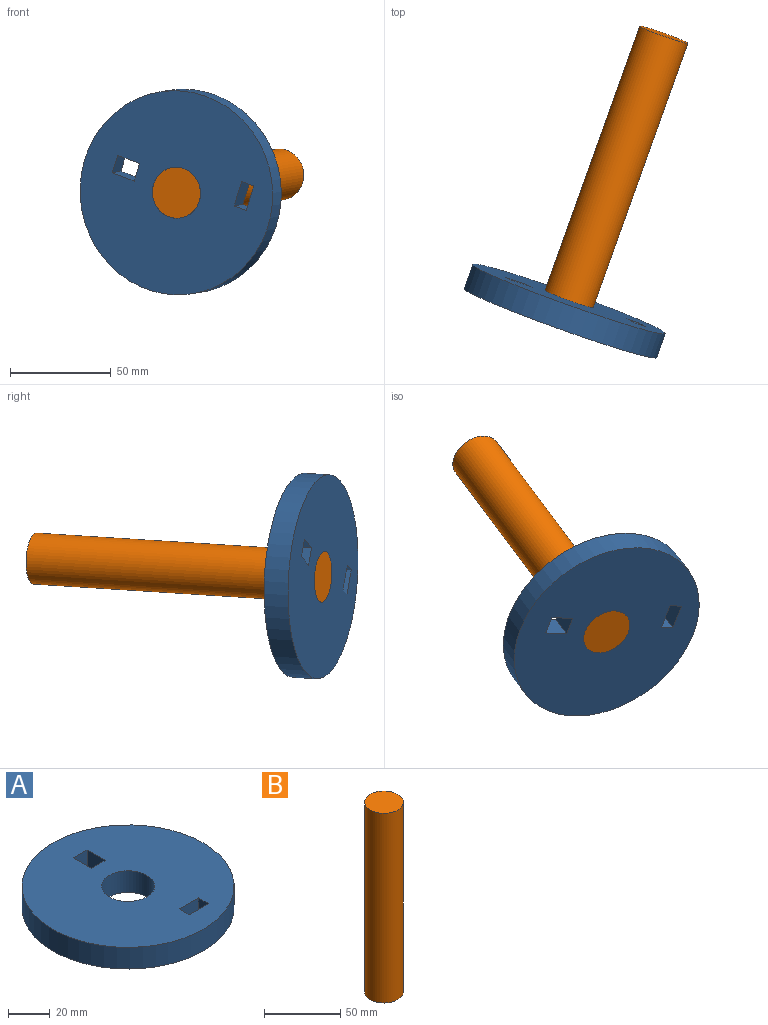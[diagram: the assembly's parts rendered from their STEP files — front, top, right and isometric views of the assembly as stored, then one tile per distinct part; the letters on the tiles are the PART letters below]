
ASSEMBLY  parts=2 mates=1
PART A: 12 faces, bbox 101.6x101.6x12.7 mm
  f0: plane 13.01x12.7mm, normal (0,1,0), area 165.2mm2, adj f1,f6,f10,f11
  f1: plane 12.7x6.7mm, normal (1,0,0), area 85.1mm2, adj f0,f2,f10,f11
  f2: plane 13.01x12.7mm, normal (0,-1,0), area 165.2mm2, adj f1,f6,f10,f11
  f3: plane 12.7x9.26mm, normal (0,1,0), area 117.6mm2, adj f4,f7,f10,f11
  f4: plane 12.7x12.22mm, normal (1,0,0), area 155.2mm2, adj f3,f5,f10,f11
  f5: plane 12.7x9.26mm, normal (0,-1,0), area 117.6mm2, adj f4,f7,f10,f11
  f6: plane 12.7x6.7mm, normal (-1,0,0), area 85.1mm2, adj f0,f2,f10,f11
  f7: plane 12.7x12.22mm, normal (-1,0,0), area 155.2mm2, adj f3,f5,f10,f11
  f8: cylinder r=12.7mm len=25.4mm, axis (0,0,-1), area 1013.4mm2, adj f10,f11
  f9: cylinder r=50.8mm len=101.6mm, axis (0,0,-1), area 4053.7mm2, adj f10,f11
  f10: plane 101.6x101.6mm, normal (0,0,1), area 7400.3mm2, adj f0,f1,f2,f3,f4,f5,f6,f7
  f11: plane 101.6x101.6mm, normal (0,0,-1), area 7400.3mm2, adj f0,f1,f2,f3,f4,f5,f6,f7
PART B: 3 faces, bbox 25.4x25.4x152.4 mm
  f0: cylinder r=12.7mm len=152.4mm, axis (0,0,-1), area 12161mm2, adj f1,f2
  f1: plane 25.4x25.4mm, normal (0,0,1), area 506.7mm2, adj f0
  f2: plane 25.4x25.4mm, normal (0,0,-1), area 506.7mm2, adj f0
PLACE A rot(axis=(0.66,-0.66,0.37),103.4deg) t=(-31.99,-44.47,32.92)mm
PLACE B rot(axis=(0.43,-0.74,0.52),116.5deg) t=(-8.47,21.17,37.07)mm fixed
MATE revolute B.f0 <-> A.f8  axis (-0.34,-0.94,-0.06) through (-34.13,-50.43,32.55)mm
